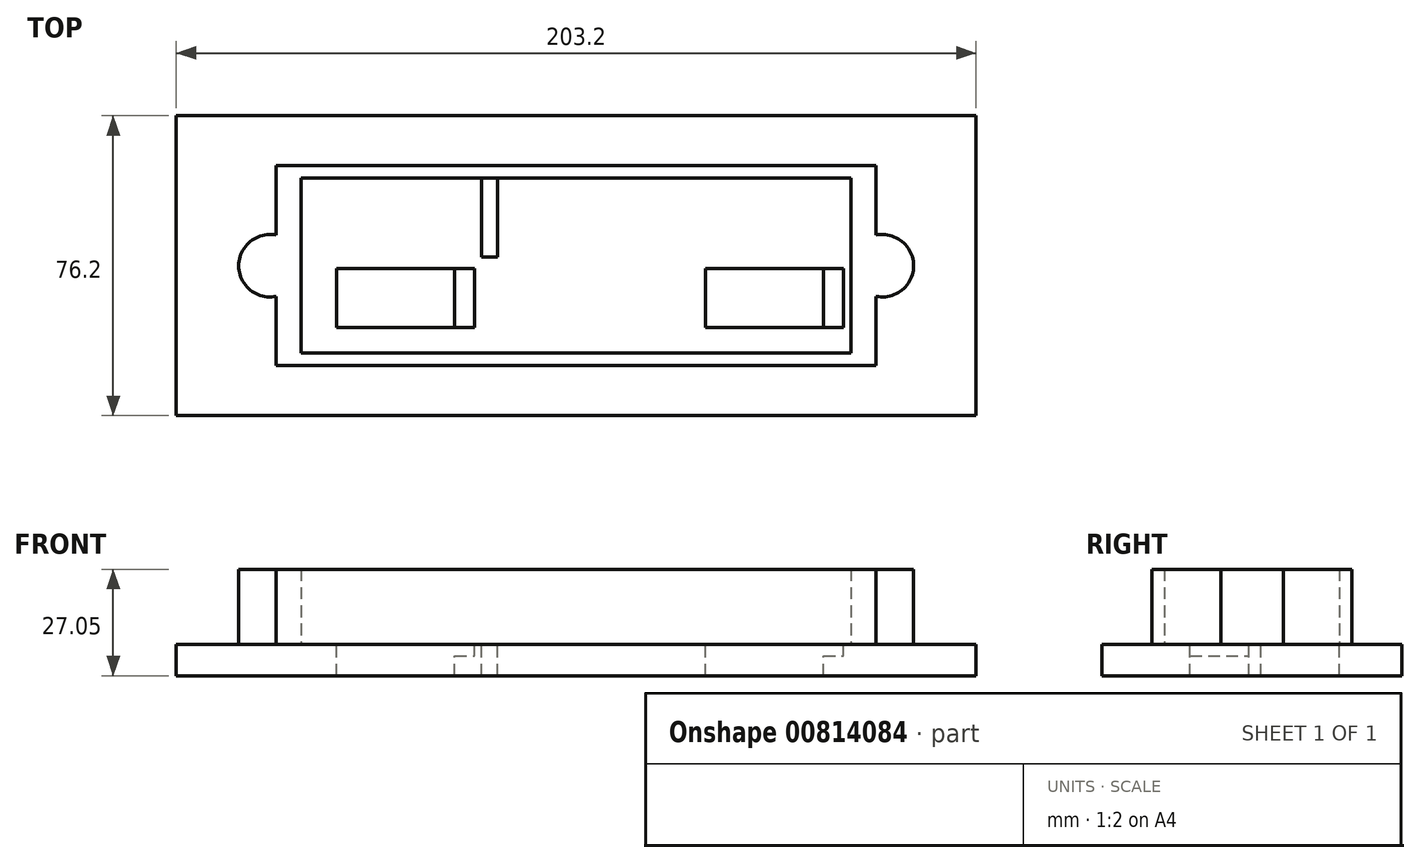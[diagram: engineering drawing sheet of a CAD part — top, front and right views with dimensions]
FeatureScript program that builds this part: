
annotation { "Feature Type Name" : "Feature", "Feature Type Description" : "" }
export const myFeature = defineFeature(function(context is Context, id is Id, definition is map)
    precondition{}
    {
        {
            var Q0;
            Q0=qCreatedBy(makeId("Top.planeOp"),FACE);
            var sketch = newSketch(context, id + "F0", { "sketchPlane" : qUnion([Q0])});
            skLineSegment(sketch, "E0.bottom", {"start": v(101.6, 38.1) * mm, "end": v(-101.6, 38.1) * mm});
            skLineSegment(sketch, "E0.top", {"start": v(101.6, -38.1) * mm, "end": v(-101.6, -38.1) * mm});
            skLineSegment(sketch, "E0.left", {"start": v(101.6, 38.1) * mm, "end": v(101.6, -38.1) * mm});
            skLineSegment(sketch, "E0.right", {"start": v(-101.6, 38.1) * mm, "end": v(-101.6, -38.1) * mm});
            skPoint(sketch, "E0.middle", {"position": v(0, 0) * mm});
            skSolve(sketch);
        }
        {
            var Q0;
            Q0 = qSketchRegion(id + "F0", true);
            extrude(context, id + "F1", {"entities" : qUnion([Q0]), "depth" : 8 * mm, "offsetDistance" : 25.4 * mm});
        }
        {
            var Q0;
            Q0=makeQuery(id+"F1.opExtrude","CAP_FACE",FACE,{"disambiguationData":[OSD([sQuery(id+"F0.wireOp",EDGE,"E0.bottom"),sQuery(id+"F0.wireOp",EDGE,"E0.top"),sQuery(id+"F0.wireOp",EDGE,"E0.left"),sQuery(id+"F0.wireOp",EDGE,"E0.right")])],"isStart":false});
            var sketch = newSketch(context, id + "F2", { "sketchPlane" : qUnion([Q0])});
            skLineSegment(sketch, "E1.bottom", {"start": v(76.2, 25.4) * mm, "end": v(-76.2, 25.4) * mm});
            skLineSegment(sketch, "E1.top", {"start": v(76.2, -25.4) * mm, "end": v(-76.2, -25.4) * mm});
            skLineSegment(sketch, "E1.left", {"start": v(76.2, 25.4) * mm, "end": v(76.2, -25.4) * mm});
            skLineSegment(sketch, "E1.right", {"start": v(-76.2, 25.4) * mm, "end": v(-76.2, -25.4) * mm});
            skPoint(sketch, "E1.middle", {"position": v(0, 0) * mm});
            skLineSegment(sketch, "E2.bottom", {"start": v(69.85, 22.23) * mm, "end": v(-69.85, 22.23) * mm});
            skLineSegment(sketch, "E2.top", {"start": v(69.85, -22.23) * mm, "end": v(-69.85, -22.23) * mm});
            skLineSegment(sketch, "E2.left", {"start": v(69.85, 22.22) * mm, "end": v(69.85, -22.23) * mm});
            skLineSegment(sketch, "E2.right", {"start": v(-69.85, 22.22) * mm, "end": v(-69.85, -22.23) * mm});
            skSolve(sketch);
        }
        {
            var Q0;
            Q0=makeQuery(id+"F2.imprint","IMPRINT",FACE,{"disambiguationData":[TD([[makeQuery(id+"F2.imprint","IMPRINT",EDGE,{"derivedFrom":sQuery(id+"F2.wireOp",EDGE,"E1.bottom")}),-1.0]])]});
            var sketch = newSketch(context, id + "F3", { "sketchPlane" : qUnion([Q0])});
            skCircle(sketch, "E3", {"center": v(-77.79, 0) * mm, "radius": 7.94 * mm});
            skCircle(sketch, "E4", {"center": v(77.79, 0) * mm, "radius": 7.94 * mm});
            skSolve(sketch);
        }
        {
            var Q0;
            Q0=makeQuery(id+"F2.imprint","IMPRINT",FACE,{"disambiguationData":[TD([[makeQuery(id+"F2.imprint","IMPRINT",EDGE,{"derivedFrom":sQuery(id+"F2.wireOp",EDGE,"E1.bottom")}),1.0]])]});
            var Q1;
            {var subQ0=sQuery(id+"F3.wireOp",EDGE,"E3");var subQ1=makeQuery(id+"F2.imprint","IMPRINT",EDGE,{"derivedFrom":sQuery(id+"F2.wireOp",EDGE,"E1.right")});var subQ2=makeQuery(id+"F3.imprint","INTERSECT",VERTEX,{"disambiguationData":[OD(0.0)],"derivedFrom":[subQ1,subQ0]});Q1=makeQuery(id+"F3.imprint","IMPRINT",FACE,{"disambiguationData":[TD([[makeQuery(id+"F3.imprint","IMPRINT",EDGE,{"disambiguationData":[TD([[subQ2,-1.0]])],"derivedFrom":subQ0}),1.0]])]});}
            var Q2;
            {var subQ0=sQuery(id+"F3.wireOp",EDGE,"E4");var subQ1=makeQuery(id+"F2.imprint","IMPRINT",EDGE,{"derivedFrom":sQuery(id+"F2.wireOp",EDGE,"E1.left")});var subQ2=makeQuery(id+"F3.imprint","INTERSECT",VERTEX,{"disambiguationData":[OD(0.0)],"derivedFrom":[subQ1,subQ0]});Q2=makeQuery(id+"F3.imprint","IMPRINT",FACE,{"disambiguationData":[TD([[makeQuery(id+"F3.imprint","IMPRINT",EDGE,{"disambiguationData":[TD([[subQ2,1.0]])],"derivedFrom":subQ0}),1.0]])]});}
            extrude(context, id + "F4", {"entities" : qUnion([Q0, Q1, Q2]), "operationType" : NewBodyOperationType.ADD, "depth" : 19.05 * mm, "offsetDistance" : 25.4 * mm});
        }
        {
            var Q0;
            Q0=makeQuery(id+"F2.imprint","IMPRINT",FACE,{"disambiguationData":[TD([[makeQuery(id+"F2.imprint","IMPRINT",EDGE,{"derivedFrom":sQuery(id+"F2.wireOp",EDGE,"E2.bottom")}),1.0]])]});
            var sketch = newSketch(context, id + "F5", { "sketchPlane" : qUnion([Q0])});
            skLineSegment(sketch, "E5.bottom", {"start": v(-25.85, -20.23) * mm, "end": v(-67.85, -20.23) * mm, "construction": true});
            skLineSegment(sketch, "E5.top", {"start": v(-25.85, 3.77) * mm, "end": v(-67.85, 3.77) * mm, "construction": true});
            skLineSegment(sketch, "E5.left", {"start": v(-25.85, -20.23) * mm, "end": v(-25.85, 3.77) * mm, "construction": true});
            skLineSegment(sketch, "E5.right", {"start": v(-67.85, -20.23) * mm, "end": v(-67.85, 3.77) * mm, "construction": true});
            skPoint(sketch, "E5.middle", {"position": v(-46.85, -8.23) * mm});
            skLineSegment(sketch, "E6.bottom", {"start": v(25.85, -20.23) * mm, "end": v(67.85, -20.22) * mm, "construction": true});
            skLineSegment(sketch, "E6.top", {"start": v(25.85, 3.78) * mm, "end": v(67.85, 3.78) * mm, "construction": true});
            skLineSegment(sketch, "E6.left", {"start": v(25.85, -20.23) * mm, "end": v(25.85, 3.78) * mm, "construction": true});
            skLineSegment(sketch, "E6.right", {"start": v(67.85, -20.23) * mm, "end": v(67.85, 3.78) * mm, "construction": true});
            skPoint(sketch, "E6.middle", {"position": v(46.85, -8.22) * mm});
            skLineSegment(sketch, "E7.bottom", {"start": v(-60.85, -15.73) * mm, "end": v(-30.85, -15.73) * mm});
            skLineSegment(sketch, "E7.top", {"start": v(-60.85, -0.73) * mm, "end": v(-30.85, -0.73) * mm});
            skLineSegment(sketch, "E7.left", {"start": v(-60.85, -15.73) * mm, "end": v(-60.85, -0.73) * mm});
            skLineSegment(sketch, "E7.right", {"start": v(-30.85, -15.73) * mm, "end": v(-30.85, -0.73) * mm});
            skPoint(sketch, "E7.middle", {"position": v(-45.85, -8.23) * mm});
            skLineSegment(sketch, "E8.bottom", {"start": v(62.85, -15.72) * mm, "end": v(32.85, -15.72) * mm});
            skLineSegment(sketch, "E8.top", {"start": v(62.85, -0.72) * mm, "end": v(32.85, -0.73) * mm});
            skLineSegment(sketch, "E8.left", {"start": v(62.85, -15.72) * mm, "end": v(62.85, -0.72) * mm});
            skLineSegment(sketch, "E8.right", {"start": v(32.85, -15.72) * mm, "end": v(32.85, -0.73) * mm});
            skPoint(sketch, "E8.middle", {"position": v(47.85, -8.22) * mm});
            skLineSegment(sketch, "E9.bottom", {"start": v(20, -12.77) * mm, "end": v(-20, -12.78) * mm, "construction": true});
            skLineSegment(sketch, "E9.top", {"start": v(20, 27.23) * mm, "end": v(-20, 27.23) * mm, "construction": true});
            skLineSegment(sketch, "E9.left", {"start": v(20, -12.77) * mm, "end": v(20, 27.23) * mm, "construction": true});
            skLineSegment(sketch, "E9.right", {"start": v(-20, -12.78) * mm, "end": v(-20, 27.23) * mm, "construction": true});
            skPoint(sketch, "E9.middle", {"position": v(0, 7.23) * mm});
            skLineSegment(sketch, "E10.bottom", {"start": v(-20, 22.23) * mm, "end": v(-24, 22.23) * mm});
            skLineSegment(sketch, "E10.top", {"start": v(-20, 2.23) * mm, "end": v(-24, 2.23) * mm});
            skLineSegment(sketch, "E10.left", {"start": v(-20, 22.23) * mm, "end": v(-20, 2.23) * mm});
            skLineSegment(sketch, "E10.right", {"start": v(-24, 22.23) * mm, "end": v(-24, 2.23) * mm});
            skPoint(sketch, "E10.middle", {"position": v(-22, 12.23) * mm});
            skSolve(sketch);
        }
        {
            var Q0;
            Q0=makeQuery(id+"F5.imprint","IMPRINT",FACE,{"disambiguationData":[TD([[makeQuery(id+"F5.imprint","IMPRINT",EDGE,{"derivedFrom":sQuery(id+"F5.wireOp",EDGE,"E8.bottom")}),-1.0]])]});
            var Q1;
            Q1=makeQuery(id+"F5.imprint","IMPRINT",FACE,{"disambiguationData":[TD([[makeQuery(id+"F5.imprint","IMPRINT",EDGE,{"derivedFrom":sQuery(id+"F5.wireOp",EDGE,"E7.bottom")}),1.0]])]});
            extrude(context, id + "F6", {"entities" : qUnion([Q0, Q1]), "operationType" : NewBodyOperationType.REMOVE, "endBound" : BoundingType.UP_TO_NEXT, "oppositeDirection" : true, "depth" : 25.4 * mm, "offsetDistance" : 25.4 * mm});
        }
        {
            var Q0;
            Q0=makeQuery(id+"F5.imprint","IMPRINT",FACE,{"disambiguationData":[TD([[makeQuery(id+"F5.imprint","IMPRINT",EDGE,{"derivedFrom":sQuery(id+"F5.wireOp",EDGE,"E10.bottom")}),1.0]])]});
            extrude(context, id + "F7", {"entities" : qUnion([Q0]), "operationType" : NewBodyOperationType.REMOVE, "endBound" : BoundingType.UP_TO_NEXT, "oppositeDirection" : true, "depth" : 25.4 * mm, "offsetDistance" : 25.4 * mm});
        }
        {
            var Q0;
            Q0=makeQuery(id+"F5.imprint","IMPRINT",FACE,{"disambiguationData":[TD([[makeQuery(id+"F5.imprint","IMPRINT",EDGE,{"derivedFrom":sQuery(id+"F5.wireOp",EDGE,"E7.bottom")}),-1.0]])]});
            var sketch = newSketch(context, id + "F8", { "sketchPlane" : qUnion([Q0])});
            skLineSegment(sketch, "E11.0", {"start": v(-30.85, -15.73) * mm, "end": v(-30.85, -0.73) * mm});
            skLineSegment(sketch, "E12", {"start": v(-30.85, -15.73) * mm, "end": v(-25.85, -15.73) * mm});
            skLineSegment(sketch, "E13", {"start": v(-25.85, -15.73) * mm, "end": v(-25.85, -0.73) * mm});
            skLineSegment(sketch, "E14", {"start": v(-25.85, -0.73) * mm, "end": v(-30.85, -0.73) * mm});
            skLineSegment(sketch, "E15.0", {"start": v(-25.85, -20.23) * mm, "end": v(-25.85, 3.77) * mm, "construction": true});
            skLineSegment(sketch, "E16.0", {"start": v(62.85, -15.72) * mm, "end": v(62.85, -0.72) * mm});
            skLineSegment(sketch, "E17.0", {"start": v(67.85, -20.23) * mm, "end": v(67.85, 3.78) * mm, "construction": true});
            skLineSegment(sketch, "E18", {"start": v(62.85, -15.72) * mm, "end": v(67.85, -15.72) * mm});
            skLineSegment(sketch, "E19", {"start": v(67.85, -15.72) * mm, "end": v(67.85, -0.72) * mm});
            skLineSegment(sketch, "E20", {"start": v(67.85, -0.72) * mm, "end": v(62.85, -0.72) * mm});
            skSolve(sketch);
        }
        {
            var Q0;
            Q0=makeQuery(id+"F8.imprint","IMPRINT",FACE,{"disambiguationData":[TD([[makeQuery(id+"F8.imprint","IMPRINT",EDGE,{"derivedFrom":sQuery(id+"F8.wireOp",EDGE,"E16.0")}),-1.0]])]});
            var Q1;
            Q1=makeQuery(id+"F8.imprint","IMPRINT",FACE,{"disambiguationData":[TD([[makeQuery(id+"F8.imprint","IMPRINT",EDGE,{"derivedFrom":sQuery(id+"F8.wireOp",EDGE,"E11.0")}),-1.0]])]});
            extrude(context, id + "F9", {"entities" : qUnion([Q0, Q1]), "operationType" : NewBodyOperationType.REMOVE, "oppositeDirection" : true, "depth" : 3 * mm, "offsetDistance" : 25.4 * mm});
        }
    });
